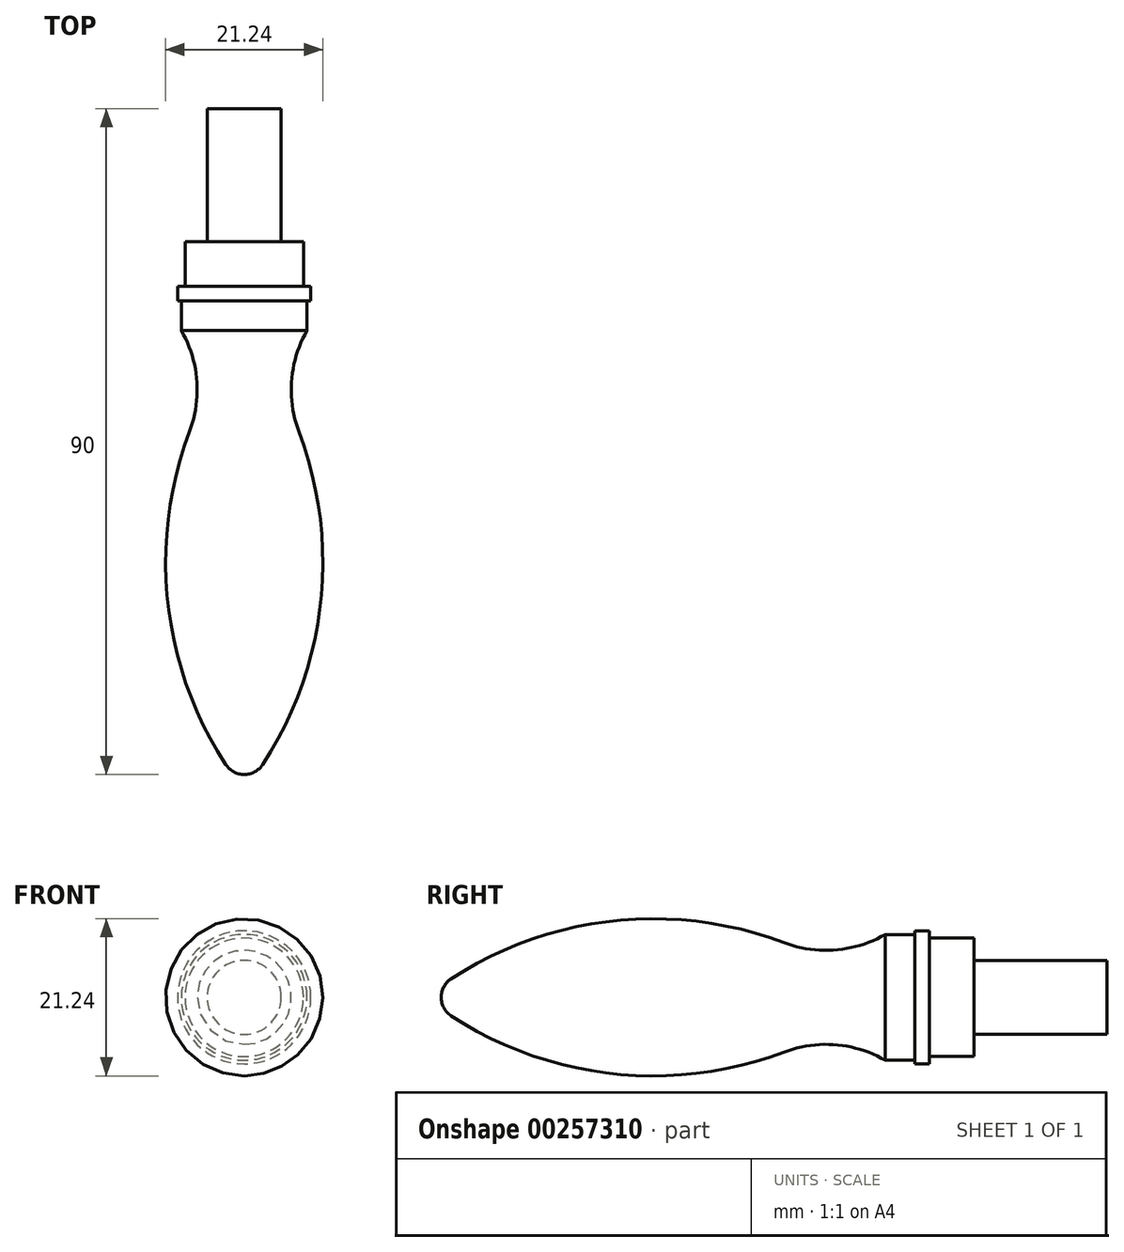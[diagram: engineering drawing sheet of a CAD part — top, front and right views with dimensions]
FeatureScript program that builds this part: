
annotation { "Feature Type Name" : "Feature", "Feature Type Description" : "" }
export const myFeature = defineFeature(function(context is Context, id is Id, definition is map)
    precondition{}
    {
        {
            var Q0;
            Q0=qCreatedBy(makeId("Right.planeOp"),FACE);
            var sketch = newSketch(context, id + "F0", { "sketchPlane" : qUnion([Q0])});
            skLineSegment(sketch, "E0", {"start": v(0, 0) * mm, "end": v(0, 5) * mm});
            skLineSegment(sketch, "E1", {"start": v(0, 5) * mm, "end": v(-18, 5) * mm});
            skLineSegment(sketch, "E2", {"start": v(-24, 8) * mm, "end": v(-24, 9) * mm});
            skLineSegment(sketch, "E3", {"start": v(-24, 9) * mm, "end": v(-26, 9) * mm});
            skLineSegment(sketch, "E4", {"start": v(-26, 9) * mm, "end": v(-26, 8.5) * mm});
            skLineSegment(sketch, "E5", {"start": v(-26, 8.5) * mm, "end": v(-30, 8.5) * mm});
            skLineSegment(sketch, "E6", {"start": v(-24, 8) * mm, "end": v(-18, 8) * mm});
            skLineSegment(sketch, "E7", {"start": v(-18, 8) * mm, "end": v(-18, 5) * mm});
            skArc(sketch, "E8", {"start": v(-43.66, 7.4) * mm, "mid": v(-36.7, 6.4) * mm, "end": v(-30, 8.5) * mm});
            skArc(sketch, "E9", {"start": v(-43.66, 7.4) * mm, "mid": v(-66.73, 10.33) * mm, "end": v(-88.64, 2.51) * mm});
            skLineSegment(sketch, "E10", {"start": v(-92.15, 0) * mm, "end": v(0, 0) * mm, "construction": true});
            skArc(sketch, "E11", {"start": v(-88.64, 2.51) * mm, "mid": v(-89.64, 1.43) * mm, "end": v(-90, 0) * mm});
            skLineSegment(sketch, "E12", {"start": v(-90, 0) * mm, "end": v(0, 0) * mm});
            skSolve(sketch);
        }
        {
            var Q0;
            Q0=makeQuery(id+"F0.imprint","IMPRINT",FACE,{"disambiguationData":[TD([[makeQuery(id+"F0.imprint","IMPRINT",EDGE,{"derivedFrom":sQuery(id+"F0.wireOp",EDGE,"E0")}),1.0]])]});
            var Q1;
            Q1=sQuery(id+"F0.wireOp",EDGE,"E10");
            revolve(context, id + "F1", {"entities" : qUnion([Q0]), "axis" : qUnion([Q1]), "revolveType" : RevolveType.FULL});
        }
    });
